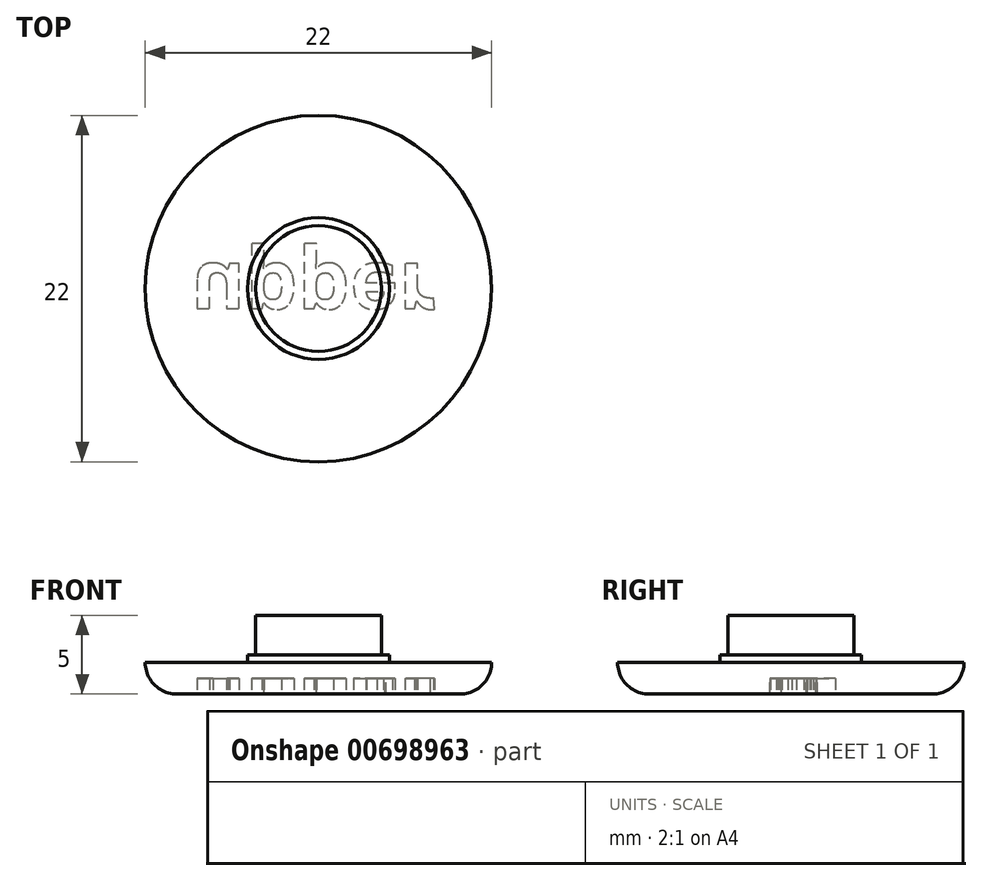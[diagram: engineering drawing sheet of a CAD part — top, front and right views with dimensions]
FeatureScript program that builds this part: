
annotation { "Feature Type Name" : "Feature", "Feature Type Description" : "" }
export const myFeature = defineFeature(function(context is Context, id is Id, definition is map)
    precondition{}
    {
        {
            var Q0;
            Q0=qCreatedBy(makeId("Top.planeOp"),FACE);
            var sketch = newSketch(context, id + "F0", { "sketchPlane" : qUnion([Q0])});
            skCircle(sketch, "E0", {"center": v(-124.76, 13.61) * mm, "radius": 11 * mm});
            skSolve(sketch);
        }
        {
            var Q0;
            Q0=makeQuery(id+"F0.imprint","IMPRINT",FACE,{"disambiguationData":[TD([[makeQuery(id+"F0.imprint","IMPRINT",EDGE,{"derivedFrom":sQuery(id+"F0.wireOp",EDGE,"E0")}),1.0]])]});
            extrude(context, id + "F1", {"entities" : qUnion([Q0]), "depth" : 2 * mm, "offsetDistance" : 25 * mm});
        }
        {
            var Q0;
            Q0=makeQuery(id+"F1.opExtrude","CAP_FACE",FACE,{"disambiguationData":[OSD([sQuery(id+"F0.wireOp",EDGE,"E0")])],"isStart":false});
            var sketch = newSketch(context, id + "F2", { "sketchPlane" : qUnion([Q0])});
            skCircle(sketch, "E1", {"center": v(-124.76, 13.61) * mm, "radius": 4.5 * mm});
            skSolve(sketch);
        }
        {
            var Q0;
            Q0=makeQuery(id+"F2.imprint","IMPRINT",FACE,{"disambiguationData":[TD([[makeQuery(id+"F2.imprint","IMPRINT",EDGE,{"derivedFrom":sQuery(id+"F2.wireOp",EDGE,"E1")}),1.0]])]});
            extrude(context, id + "F3", {"entities" : qUnion([Q0]), "operationType" : NewBodyOperationType.ADD, "depth" : 0.5 * mm, "offsetDistance" : 25 * mm});
        }
        {
            var Q0;
            Q0=makeQuery(id+"F3.opExtrude","CAP_FACE",FACE,{"disambiguationData":[OSD([sQuery(id+"F2.wireOp",EDGE,"E1")])],"isStart":false});
            var sketch = newSketch(context, id + "F4", { "sketchPlane" : qUnion([Q0])});
            skCircle(sketch, "E2", {"center": v(-124.76, 13.61) * mm, "radius": 4 * mm});
            skSolve(sketch);
        }
        {
            var Q0;
            Q0=makeQuery(id+"F4.imprint","IMPRINT",FACE,{"disambiguationData":[TD([[makeQuery(id+"F4.imprint","IMPRINT",EDGE,{"derivedFrom":sQuery(id+"F4.wireOp",EDGE,"E2")}),1.0]])]});
            extrude(context, id + "F5", {"entities" : qUnion([Q0]), "operationType" : NewBodyOperationType.ADD, "depth" : 2.5 * mm, "offsetDistance" : 25 * mm});
        }
        {
            var Q0;
            Q0=makeQuery(id+"F1.opExtrude","CAP_EDGE",EDGE,{"disambiguationData":[OSD([sQuery(id+"F0.wireOp",EDGE,"E0")])],"isStart":true});
            var Q1;
            Q1=makeQuery(id+"F3.opExtrude","CAP_EDGE",EDGE,{"disambiguationData":[OSD([sQuery(id+"F2.wireOp",EDGE,"E1")])],"isStart":true});
            fillet(context, id + "F6", {"entities" : qUnion([Q0, Q1]), "radius" : 2 * mm, "tangentPropagation" : true, "allowEdgeOverflow" : false});
        }
        {
            var Q0;
            Q0=makeQuery(id+"F1.opExtrude","CAP_FACE",FACE,{"disambiguationData":[OSD([sQuery(id+"F0.wireOp",EDGE,"E0")])],"isStart":true});
            var sketch = newSketch(context, id + "F7", { "sketchPlane" : qUnion([Q0])});
            skText(sketch, "E3", { "text": "upper ", "fontName": "OpenSans-Bold.ttf"});
            const initialGuessF7  = {"E3": [-0.13285, -0.0152, 1, 0, 0.00378]};
            skSetInitialGuess(sketch, initialGuessF7);
            skSolve(sketch);
        }
        {
            var Q0;
            Q0 = qSketchRegion(id + "F7", true);
            extrude(context, id + "F8", {"entities" : qUnion([Q0]), "operationType" : NewBodyOperationType.REMOVE, "oppositeDirection" : true, "depth" : 1 * mm, "offsetDistance" : 25 * mm});
        }
    });
